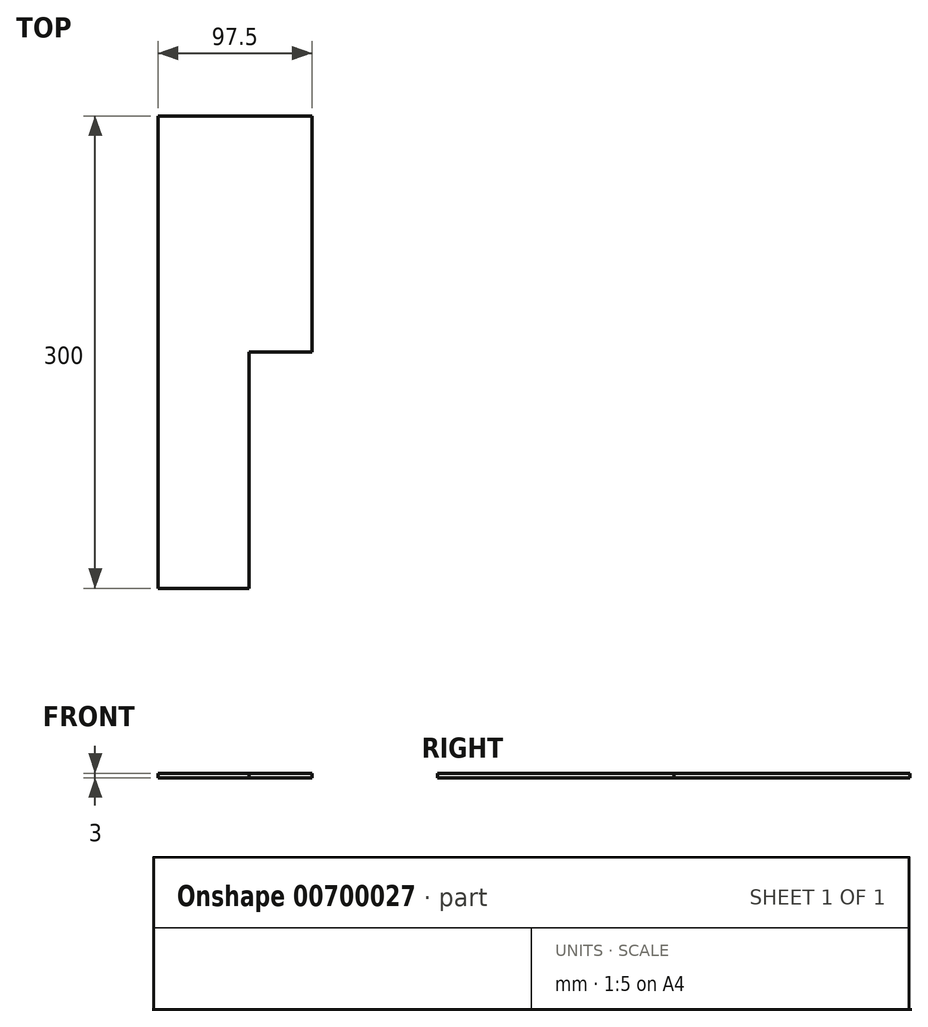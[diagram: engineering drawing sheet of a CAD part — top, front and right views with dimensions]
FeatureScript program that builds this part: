
annotation { "Feature Type Name" : "Feature", "Feature Type Description" : "" }
export const myFeature = defineFeature(function(context is Context, id is Id, definition is map)
    precondition{}
    {
        {
            var Q0;
            Q0=qCreatedBy(makeId("Top.planeOp"),FACE);
            var sketch = newSketch(context, id + "F0", { "sketchPlane" : qUnion([Q0])});
            skLineSegment(sketch, "E0.bottom", {"start": v(48.75, -150) * mm, "end": v(-48.75, -150) * mm});
            skLineSegment(sketch, "E0.top", {"start": v(48.75, 150) * mm, "end": v(-48.75, 150) * mm});
            skLineSegment(sketch, "E0.left", {"start": v(48.75, -150) * mm, "end": v(48.75, 150) * mm});
            skLineSegment(sketch, "E0.right", {"start": v(-48.75, -150) * mm, "end": v(-48.75, 150) * mm});
            skPoint(sketch, "E0.middle", {"position": v(0, 0) * mm});
            skSolve(sketch);
        }
        {
            var Q0;
            Q0 = qSketchRegion(id + "F0", true);
            extrude(context, id + "F1", {"entities" : qUnion([Q0]), "depth" : 3 * mm, "offsetDistance" : 25 * mm});
        }
        {
            var Q0;
            Q0=makeQuery(id+"F1.opExtrude","CAP_FACE",FACE,{"disambiguationData":[OSD([sQuery(id+"F0.wireOp",EDGE,"E0.bottom"),sQuery(id+"F0.wireOp",EDGE,"E0.top"),sQuery(id+"F0.wireOp",EDGE,"E0.left"),sQuery(id+"F0.wireOp",EDGE,"E0.right")])],"isStart":false});
            var sketch = newSketch(context, id + "F2", { "sketchPlane" : qUnion([Q0])});
            skLineSegment(sketch, "E1.bottom", {"start": v(48.75, -150) * mm, "end": v(8.75, -150) * mm});
            skLineSegment(sketch, "E1.top", {"start": v(48.75, 0) * mm, "end": v(8.75, 0) * mm});
            skLineSegment(sketch, "E1.left", {"start": v(48.75, -150) * mm, "end": v(48.75, 0) * mm});
            skLineSegment(sketch, "E1.right", {"start": v(8.75, -150) * mm, "end": v(8.75, 0) * mm});
            skSolve(sketch);
        }
        {
            var Q0;
            Q0 = qSketchRegion(id + "F2", true);
            extrude(context, id + "F3", {"entities" : qUnion([Q0]), "operationType" : NewBodyOperationType.REMOVE, "endBound" : BoundingType.UP_TO_NEXT, "oppositeDirection" : true, "depth" : 25 * mm, "offsetDistance" : 25 * mm});
        }
    });
